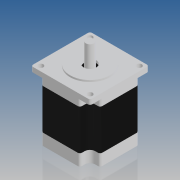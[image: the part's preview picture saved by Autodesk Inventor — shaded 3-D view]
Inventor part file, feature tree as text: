
AUTODESK INVENTOR PART (.ipt)
format: ipt  version: 2017 (Build 210142000, 142)  size: 332,288 bytes
history: native  units: mm
features: other x6, sketch x5, extrude x4, plane x2, split x2, shell x2, fillet x1, revolve x1
ambient origin geometry x8: Origin, YZ Plane, XZ Plane, XY Plane, X Axis, Y Axis, Z Axis, Center Point
bodies: Body1 (feature_tree), Body2 (feature_tree), Body3 (feature_tree), Body4 (feature_tree)
feature tree (23):
  other  "Sólido1"
  extrude  "Extrusión1"  Depth=2.0mm
  extrude  "Extrusión2"  Depth=61.609459mm
  extrude  "Extrusión3"  Depth=4.7mm TaperAngle=0.0deg
  fillet  "Empalme1"  Radius=37.0mm
  plane  "Plano de trabajo1"
  plane  "Plano de trabajo2"
  split  "Dividir1"
  split  "Dividir2"
  shell  "Vaciado1"  Thickness=56.0mm
  shell  "Vaciado2"  Thickness=38.0mm
  revolve  "Revolución1"  [1 undecoded]
  extrude  "Extrusión4"  Depth=2.0mm
  sketch  "Boceto1"  dims[d0=56.4mm d1=2.0mm]
  sketch  "Boceto2"  dims[d2=5.0mm d3=61.609459mm]
  sketch  "Boceto3"  dims[d4=12.0mm d5=4.7mm d6=0.0mm d7=37.0mm d8=56.0mm d9=0.0mm d10=38.0mm]
  sketch  "Boceto4"  dims[d11=1.6mm d12=0.0mm d13=-11.0mm]
  other  "Sólido6"
  sketch  "Boceto5"  dims[d14=-11.0mm d15=2.0mm d16=8.0mm d17=19.0mm d18=90.0deg d19=7.4mm d20=2.0mm d21=10.0mm d22=0.0mm d23=47.1mm d24=4.4mm d25=2.4mm d26=2.0mm]
  other  "Sólido2"
  other  "Sólido3"
  other  "Sólido4"
  other  "Sólido5"
note: 1 required parameter value undecoded (feature->parameter linkage not recoverable at this tier; creation-order binding heuristic only, values carry confidence <= 0.55)
